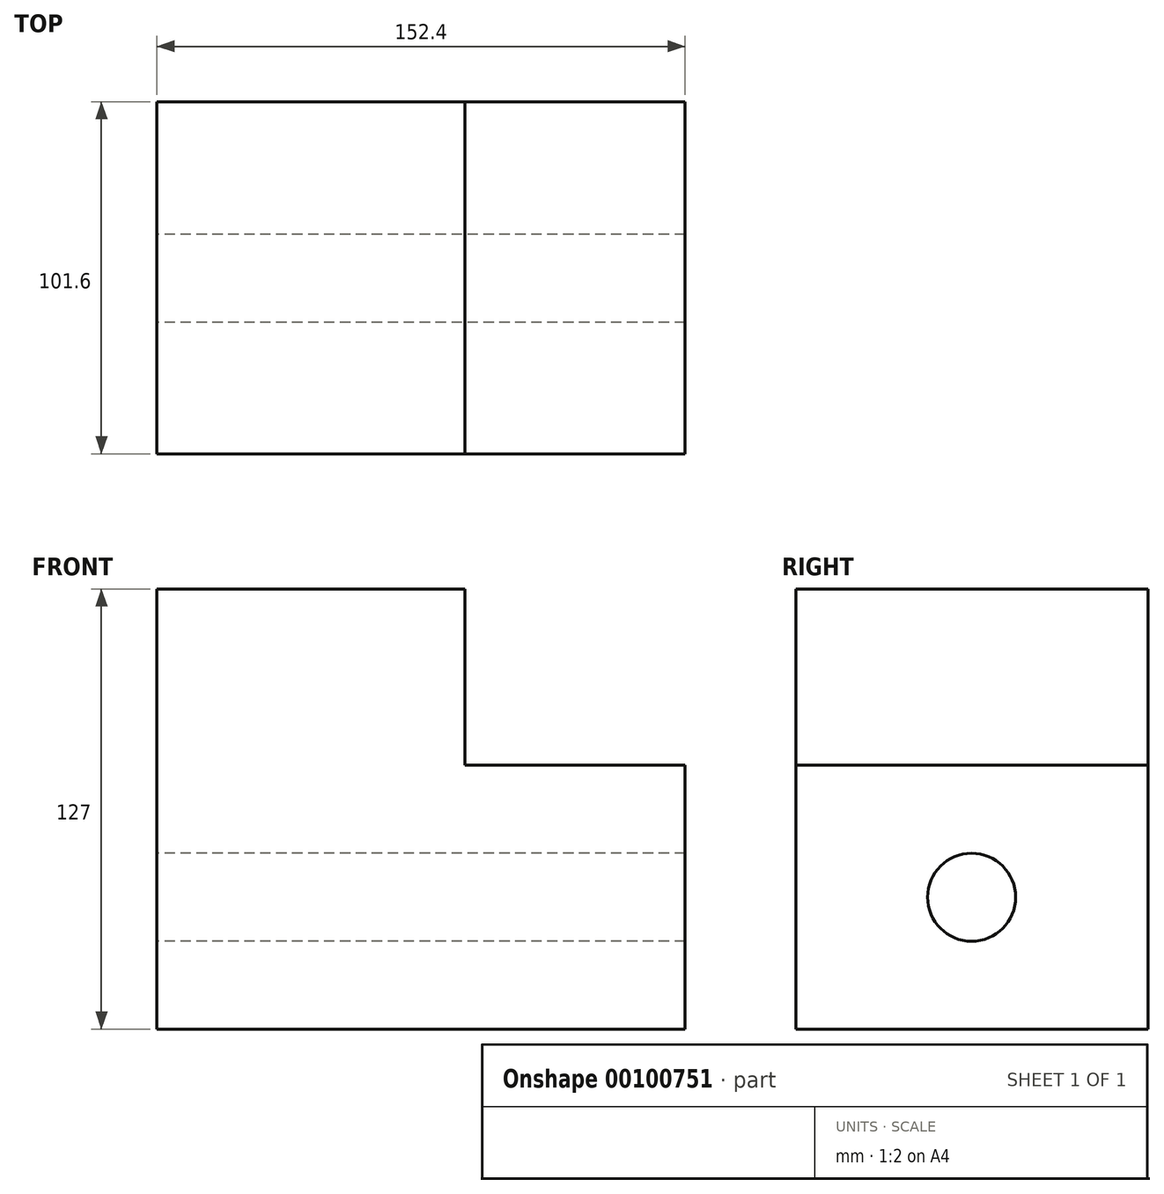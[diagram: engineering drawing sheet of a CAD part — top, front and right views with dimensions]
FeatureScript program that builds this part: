
annotation { "Feature Type Name" : "Feature", "Feature Type Description" : "" }
export const myFeature = defineFeature(function(context is Context, id is Id, definition is map)
    precondition{}
    {
        {
            var Q0;
            Q0=qCreatedBy(makeId("Front.planeOp"),FACE);
            var sketch = newSketch(context, id + "F0", { "sketchPlane" : qUnion([Q0])});
            skLineSegment(sketch, "E0", {"start": v(0, 0) * mm, "end": v(152.4, 0) * mm});
            skLineSegment(sketch, "E1", {"start": v(152.4, 0) * mm, "end": v(152.4, 127) * mm});
            skLineSegment(sketch, "E2", {"start": v(152.4, 127) * mm, "end": v(0, 127) * mm});
            skLineSegment(sketch, "E3", {"start": v(0, 127) * mm, "end": v(0, 0) * mm});
            skSolve(sketch);
        }
        {
            var Q0;
            Q0=makeQuery(id+"F0.imprint","IMPRINT",FACE,{"disambiguationData":[TD([[makeQuery(id+"F0.imprint","IMPRINT",EDGE,{"derivedFrom":sQuery(id+"F0.wireOp",EDGE,"E0")}),1.0]])]});
            extrude(context, id + "F1", {"entities" : qUnion([Q0]), "depth" : 101.6 * mm});
        }
        {
            var Q0;
            Q0=qSketchRegion(id+"F0",true);
            extrude(context, id + "F2", {"entities" : qUnion([Q0]), "operationType" : NewBodyOperationType.ADD, "depth" : 101.6 * mm});
        }
        {
            var Q0;
            Q0=makeQuery(id+"F1.opExtrude","CAP_FACE",FACE,{"disambiguationData":[OSD([sQuery(id+"F0.wireOp",EDGE,"E0"),sQuery(id+"F0.wireOp",EDGE,"E1"),sQuery(id+"F0.wireOp",EDGE,"E2"),sQuery(id+"F0.wireOp",EDGE,"E3")])],"isStart":false});
            var sketch = newSketch(context, id + "F3", { "sketchPlane" : qUnion([Q0])});
            skLineSegment(sketch, "E4.bottom", {"start": v(152.4, 127) * mm, "end": v(88.9, 127) * mm});
            skLineSegment(sketch, "E4.top", {"start": v(152.4, 76.2) * mm, "end": v(88.9, 76.2) * mm});
            skLineSegment(sketch, "E4.left", {"start": v(152.4, 127) * mm, "end": v(152.4, 76.2) * mm});
            skLineSegment(sketch, "E4.right", {"start": v(88.9, 127) * mm, "end": v(88.9, 76.2) * mm});
            skSolve(sketch);
        }
        {
            var Q0;
            Q0=makeQuery(id+"F3.imprint","IMPRINT",FACE,{"disambiguationData":[TD([[makeQuery(id+"F3.imprint","IMPRINT",EDGE,{"derivedFrom":sQuery(id+"F3.wireOp",EDGE,"E4.bottom")}),1.0]])]});
            extrude(context, id + "F4", {"entities" : qUnion([Q0]), "operationType" : NewBodyOperationType.REMOVE, "endBound" : BoundingType.THROUGH_ALL, "oppositeDirection" : true, "depth" : 25.4 * mm});
        }
        {
            var Q0;
            Q0=makeQuery(id+"F1.opExtrude","SWEPT_FACE",FACE,{"disambiguationData":[OSD([sQuery(id+"F0.wireOp",EDGE,"E3")])]});
            var sketch = newSketch(context, id + "F5", { "sketchPlane" : qUnion([Q0])});
            skLineSegment(sketch, "E5.bottom", {"start": v(0, 0) * mm, "end": v(50.8, 0) * mm});
            skLineSegment(sketch, "E5.top", {"start": v(0, 38.1) * mm, "end": v(50.8, 38.1) * mm});
            skLineSegment(sketch, "E5.left", {"start": v(0, 0) * mm, "end": v(0, 38.1) * mm});
            skLineSegment(sketch, "E5.right", {"start": v(50.8, 0) * mm, "end": v(50.8, 38.1) * mm});
            skSolve(sketch);
        }
        {
            var Q0;
            {var subQ5=sQuery(id+"F5.wireOp",EDGE,"E5.top");Q0=makeQuery(id+"F5.imprint","IMPRINT",FACE,{"disambiguationData":[TD([[makeQuery(id+"F5.imprint","IMPRINT",EDGE,{"derivedFrom":subQ5}),1.0]])]});}
            var sketch = newSketch(context, id + "F6", { "sketchPlane" : qUnion([Q0])});
            skCircle(sketch, "E6", {"center": v(50.93, 38.03) * mm, "radius": 12.7 * mm});
            skSolve(sketch);
        }
        {
            var Q0;
            {var subQ0=sQuery(id+"F6.wireOp",EDGE,"E6");var subQ1=makeQuery(id+"F5.imprint","IMPRINT",EDGE,{"derivedFrom":sQuery(id+"F5.wireOp",EDGE,"E5.top")});var subQ2=makeQuery(id+"F6.imprint","INTERSECT",VERTEX,{"derivedFrom":[subQ1,subQ0]});Q0=makeQuery(id+"F6.imprint","IMPRINT",FACE,{"disambiguationData":[TD([[makeQuery(id+"F6.imprint","IMPRINT",EDGE,{"disambiguationData":[TD([[subQ2,-1.0]])],"derivedFrom":subQ0}),1.0]])]});}
            var Q1;
            {var subQ0=sQuery(id+"F6.wireOp",EDGE,"E6");var subQ1=makeQuery(id+"F5.imprint","IMPRINT",EDGE,{"derivedFrom":sQuery(id+"F5.wireOp",EDGE,"E5.top")});var subQ2=makeQuery(id+"F6.imprint","INTERSECT",VERTEX,{"derivedFrom":[subQ1,subQ0]});Q1=makeQuery(id+"F6.imprint","IMPRINT",FACE,{"disambiguationData":[TD([[makeQuery(id+"F6.imprint","IMPRINT",EDGE,{"disambiguationData":[TD([[subQ2,1.0]])],"derivedFrom":subQ0}),1.0]])]});}
            extrude(context, id + "F7", {"entities" : qUnion([Q0, Q1]), "operationType" : NewBodyOperationType.REMOVE, "endBound" : BoundingType.THROUGH_ALL, "oppositeDirection" : true, "depth" : 25.4 * mm});
        }
    });
